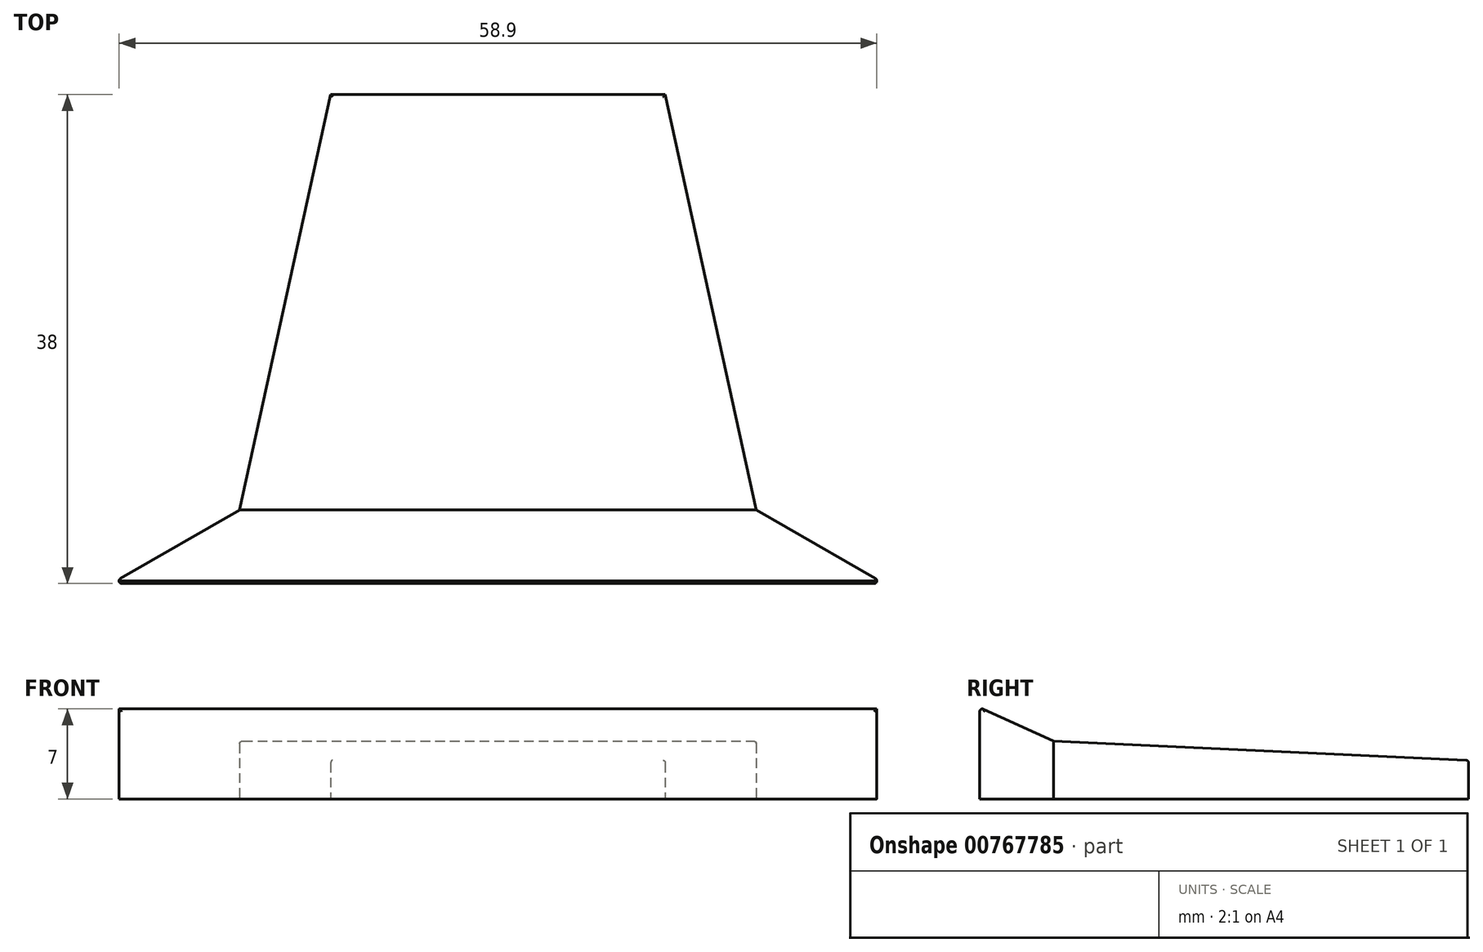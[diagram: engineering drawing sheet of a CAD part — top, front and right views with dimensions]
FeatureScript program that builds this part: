
annotation { "Feature Type Name" : "Feature", "Feature Type Description" : "" }
export const myFeature = defineFeature(function(context is Context, id is Id, definition is map)
    precondition{}
    {
        {
            var Q0;
            Q0=qCreatedBy(makeId("Top.planeOp"),FACE);
            var sketch = newSketch(context, id + "F0", { "sketchPlane" : qUnion([Q0])});
            skLineSegment(sketch, "E0", {"start": v(0, 38) * mm, "end": v(13, 38) * mm});
            skLineSegment(sketch, "E1", {"start": v(0, 0) * mm, "end": v(30, 0) * mm});
            skLineSegment(sketch, "E2", {"start": v(30, 0) * mm, "end": v(20.08, 5.73) * mm});
            skLineSegment(sketch, "E3", {"start": v(20.08, 5.73) * mm, "end": v(13, 38) * mm});
            skLineSegment(sketch, "E4.MirrorCS", {"start": v(0, 38) * mm, "end": v(-13, 38) * mm});
            skLineSegment(sketch, "E5.MirrorCS", {"start": v(-20.08, 5.73) * mm, "end": v(-13, 38) * mm});
            skLineSegment(sketch, "E6.MirrorCS", {"start": v(-30, 0) * mm, "end": v(-20.08, 5.73) * mm});
            skLineSegment(sketch, "E7.MirrorCS", {"start": v(0, 0) * mm, "end": v(-30, 0) * mm});
            skLineSegment(sketch, "E8", {"start": v(-20.08, 5.73) * mm, "end": v(20.08, 5.73) * mm});
            skSolve(sketch);
        }
        {
            var Q0;
            Q0=makeQuery(id+"F0.imprint","IMPRINT",FACE,{"disambiguationData":[TD([[makeQuery(id+"F0.imprint","IMPRINT",EDGE,{"derivedFrom":sQuery(id+"F0.wireOp",EDGE,"E0")}),-1.0]])]});
            extrude(context, id + "F1", {"entities" : qUnion([Q0]), "depth" : 3 * mm, "offsetDistance" : 25 * mm});
        }
        {
            var Q0;
            Q0=makeQuery(id+"F0.imprint","IMPRINT",FACE,{"disambiguationData":[TD([[makeQuery(id+"F0.imprint","IMPRINT",EDGE,{"derivedFrom":sQuery(id+"F0.wireOp",EDGE,"E1")}),1.0]])]});
            extrude(context, id + "F2", {"entities" : qUnion([Q0]), "operationType" : NewBodyOperationType.ADD, "depth" : 7 * mm, "offsetDistance" : 25 * mm});
        }
        {
            var Q0;
            Q0=makeQuery(id+"F2.opExtrude","CAP_EDGE",EDGE,{"disambiguationData":[OSD([sQuery(id+"F0.wireOp",EDGE,"E8")])],"isStart":false});
            chamfer(context, id + "F3", {"entities" : qUnion([Q0]), "chamferType" : ChamferType.TWO_OFFSETS, "width1" : 2.5 * mm, "oppositeDirection" : false, "width2" : 5.5 * mm, "tangentPropagation" : true});
        }
        {
            var Q0;
            Q0=makeQuery(id+"F1.opExtrude","SWEPT_FACE",FACE,{"disambiguationData":[OSD([sQuery(id+"F0.wireOp",EDGE,"E3")])]});
            cPlane(context, id + "F4", {"entities" : qUnion([Q0]), "cplaneType" : CPlaneType.OFFSET, "offset" : 0 * mm, "width" : 150 * mm, "height" : 150 * mm});
        }
        {
            var Q0;
            Q0=qCreatedBy(id+"F4.planeOp",FACE);
            var sketch = newSketch(context, id + "F5", { "sketchPlane" : qUnion([Q0])});
            skLineSegment(sketch, "E9", {"start": v(34.33, 3) * mm, "end": v(1.3, 4.5) * mm});
            skLineSegment(sketch, "E10", {"start": v(34.33, 3) * mm, "end": v(1.3, 3) * mm});
            skLineSegment(sketch, "E11", {"start": v(1.3, 4.5) * mm, "end": v(1.3, 3) * mm});
            skSolve(sketch);
        }
        {
            var Q0;
            Q0=makeQuery(id+"F1.opExtrude","SWEPT_FACE",FACE,{"disambiguationData":[OSD([sQuery(id+"F0.wireOp",EDGE,"E5.MirrorCS")])]});
            cPlane(context, id + "F6", {"entities" : qUnion([Q0]), "cplaneType" : CPlaneType.OFFSET, "offset" : 0 * mm, "width" : 150 * mm, "height" : 150 * mm});
        }
        {
            var Q0;
            Q0=qCreatedBy(id+"F6.planeOp",FACE);
            var sketch = newSketch(context, id + "F7", { "sketchPlane" : qUnion([Q0])});
            skLineSegment(sketch, "E12", {"start": v(-34.33, 3) * mm, "end": v(-1.3, 4.5) * mm});
            skLineSegment(sketch, "E13", {"start": v(-34.33, 3) * mm, "end": v(-1.3, 3) * mm});
            skLineSegment(sketch, "E14", {"start": v(-1.3, 4.5) * mm, "end": v(-1.3, 3) * mm});
            skSolve(sketch);
        }
        {
            var Q1;
            Q1=makeQuery(id+"F5.imprint","IMPRINT",FACE,{"disambiguationData":[TD([[makeQuery(id+"F5.imprint","IMPRINT",EDGE,{"derivedFrom":sQuery(id+"F5.wireOp",EDGE,"E9")}),1.0]])]});
            var Q2;
            Q2=makeQuery(id+"F7.imprint","IMPRINT",FACE,{"disambiguationData":[TD([[makeQuery(id+"F7.imprint","IMPRINT",EDGE,{"derivedFrom":sQuery(id+"F7.wireOp",EDGE,"E12")}),-1.0]])]});
            loft(context, id + "F8", {"operationType" : NewBodyOperationType.ADD, "sheetProfilesArray" : [{ "sheetProfileEntities" : qUnion([Q1]) }, { "sheetProfileEntities" : qUnion([Q2]) }]});
        }
        {
            var Q0;
            Q0=makeQuery(id+"F8.boolean.opBoolean","MERGE",EDGE,{"derivedFrom":[makeQuery(id+"F1.opExtrude","CAP_EDGE",EDGE,{"disambiguationData":[OSD([sQuery(id+"F0.wireOp",EDGE,"E0"),sQuery(id+"F0.wireOp",EDGE,"E4.MirrorCS")])],"isStart":false}),makeQuery(id+"F8.opLoft","SWEPT_EDGE",EDGE,{"disambiguationData":[OSD([sQuery(id+"F5.wireOp",EDGE,"E9"),sQuery(id+"F5.wireOp",EDGE,"E10"),sQuery(id+"F7.wireOp",EDGE,"E12"),sQuery(id+"F7.wireOp",EDGE,"E13")])]})]});
            var Q1;
            {var subQ0=sQuery(id+"F5.wireOp",EDGE,"E9");var subQ1=sQuery(id+"F5.wireOp",EDGE,"E11");var subQ2=sQuery(id+"F5.wireOp",EDGE,"E10");Q1=makeQuery(id+"F8.opLoft","MID_CAP_EDGE",EDGE,{"disambiguationData":[OSD([subQ0,subQ2,subQ1]),TDD([makeQuery(id+"F5.imprint","INTERSECT",VERTEX,{"derivedFrom":[subQ0,subQ2]}),makeQuery(id+"F5.imprint","INTERSECT",VERTEX,{"derivedFrom":[subQ0,subQ1]}),makeQuery(id+"F5.imprint","IMPRINT",EDGE,{"derivedFrom":subQ0})])],"capPos":0.0});}
            var Q2;
            Q2=makeQuery(id+"F3.opChamfer","BLEND_EDGE",EDGE,{"blendedFrom":[makeQuery(id+"F2.opExtrude","CAP_EDGE",EDGE,{"disambiguationData":[OSD([sQuery(id+"F0.wireOp",EDGE,"E8")])],"isStart":false}),makeQuery(id+"F2.opExtrude","SWEPT_FACE",FACE,{"disambiguationData":[OSD([sQuery(id+"F0.wireOp",EDGE,"E2")])]})],"blendedInto":[makeQuery(id+"F2.opExtrude","SWEPT_FACE",FACE,{"disambiguationData":[OSD([sQuery(id+"F0.wireOp",EDGE,"E2")])]})]});
            var Q3;
            {var subQ0=sQuery(id+"F7.wireOp",EDGE,"E12");var subQ1=sQuery(id+"F7.wireOp",EDGE,"E14");var subQ2=sQuery(id+"F7.wireOp",EDGE,"E13");Q3=makeQuery(id+"F8.opLoft","MID_CAP_EDGE",EDGE,{"disambiguationData":[OSD([subQ0,subQ2,subQ1]),TDD([makeQuery(id+"F7.imprint","INTERSECT",VERTEX,{"derivedFrom":[subQ0,subQ2]}),makeQuery(id+"F7.imprint","INTERSECT",VERTEX,{"derivedFrom":[subQ0,subQ1]}),makeQuery(id+"F7.imprint","IMPRINT",EDGE,{"derivedFrom":subQ0})])],"capPos":1.0});}
            var Q4;
            Q4=makeQuery(id+"F3.opChamfer","BLEND_EDGE",EDGE,{"blendedFrom":[makeQuery(id+"F2.opExtrude","CAP_EDGE",EDGE,{"disambiguationData":[OSD([sQuery(id+"F0.wireOp",EDGE,"E8")])],"isStart":false}),makeQuery(id+"F2.opExtrude","SWEPT_FACE",FACE,{"disambiguationData":[OSD([sQuery(id+"F0.wireOp",EDGE,"E6.MirrorCS")])]})],"blendedInto":[makeQuery(id+"F2.opExtrude","SWEPT_FACE",FACE,{"disambiguationData":[OSD([sQuery(id+"F0.wireOp",EDGE,"E6.MirrorCS")])]})]});
            var Q5;
            Q5=makeQuery(id+"F2.opExtrude","SWEPT_EDGE",EDGE,{"disambiguationData":[OSD([sQuery(id+"F0.wireOp",EDGE,"E6.MirrorCS"),sQuery(id+"F0.wireOp",EDGE,"E7.MirrorCS")])]});
            var Q6;
            {var subQ0=sQuery(id+"F0.wireOp",EDGE,"E8");Q6=makeQuery(id+"F3.opChamfer","BLEND_EDGE",EDGE,{"blendedFrom":[makeQuery(id+"F2.opExtrude","CAP_EDGE",EDGE,{"disambiguationData":[OSD([subQ0])],"isStart":false}),makeQuery(id+"F2.opExtrude","CAP_FACE",FACE,{"disambiguationData":[OSD([sQuery(id+"F0.wireOp",EDGE,"E1"),sQuery(id+"F0.wireOp",EDGE,"E2"),sQuery(id+"F0.wireOp",EDGE,"E6.MirrorCS"),sQuery(id+"F0.wireOp",EDGE,"E7.MirrorCS"),subQ0])],"isStart":false})],"blendedInto":[makeQuery(id+"F2.opExtrude","CAP_FACE",FACE,{"disambiguationData":[OSD([sQuery(id+"F0.wireOp",EDGE,"E1"),sQuery(id+"F0.wireOp",EDGE,"E2"),sQuery(id+"F0.wireOp",EDGE,"E6.MirrorCS"),sQuery(id+"F0.wireOp",EDGE,"E7.MirrorCS"),subQ0])],"isStart":false})]});}
            var Q7;
            Q7=makeQuery(id+"F2.opExtrude","CAP_EDGE",EDGE,{"disambiguationData":[OSD([sQuery(id+"F0.wireOp",EDGE,"E1"),sQuery(id+"F0.wireOp",EDGE,"E7.MirrorCS")])],"isStart":false});
            var Q8;
            Q8=makeQuery(id+"F2.opExtrude","SWEPT_EDGE",EDGE,{"disambiguationData":[OSD([sQuery(id+"F0.wireOp",EDGE,"E1"),sQuery(id+"F0.wireOp",EDGE,"E2")])]});
            fillet(context, id + "F9", {"entities" : qUnion([Q0, Q1, Q2, Q3, Q4, Q5, Q6, Q7, Q8]), "radius" : 0.2 * mm, "tangentPropagation" : true, "allowEdgeOverflow" : false});
        }
    });
